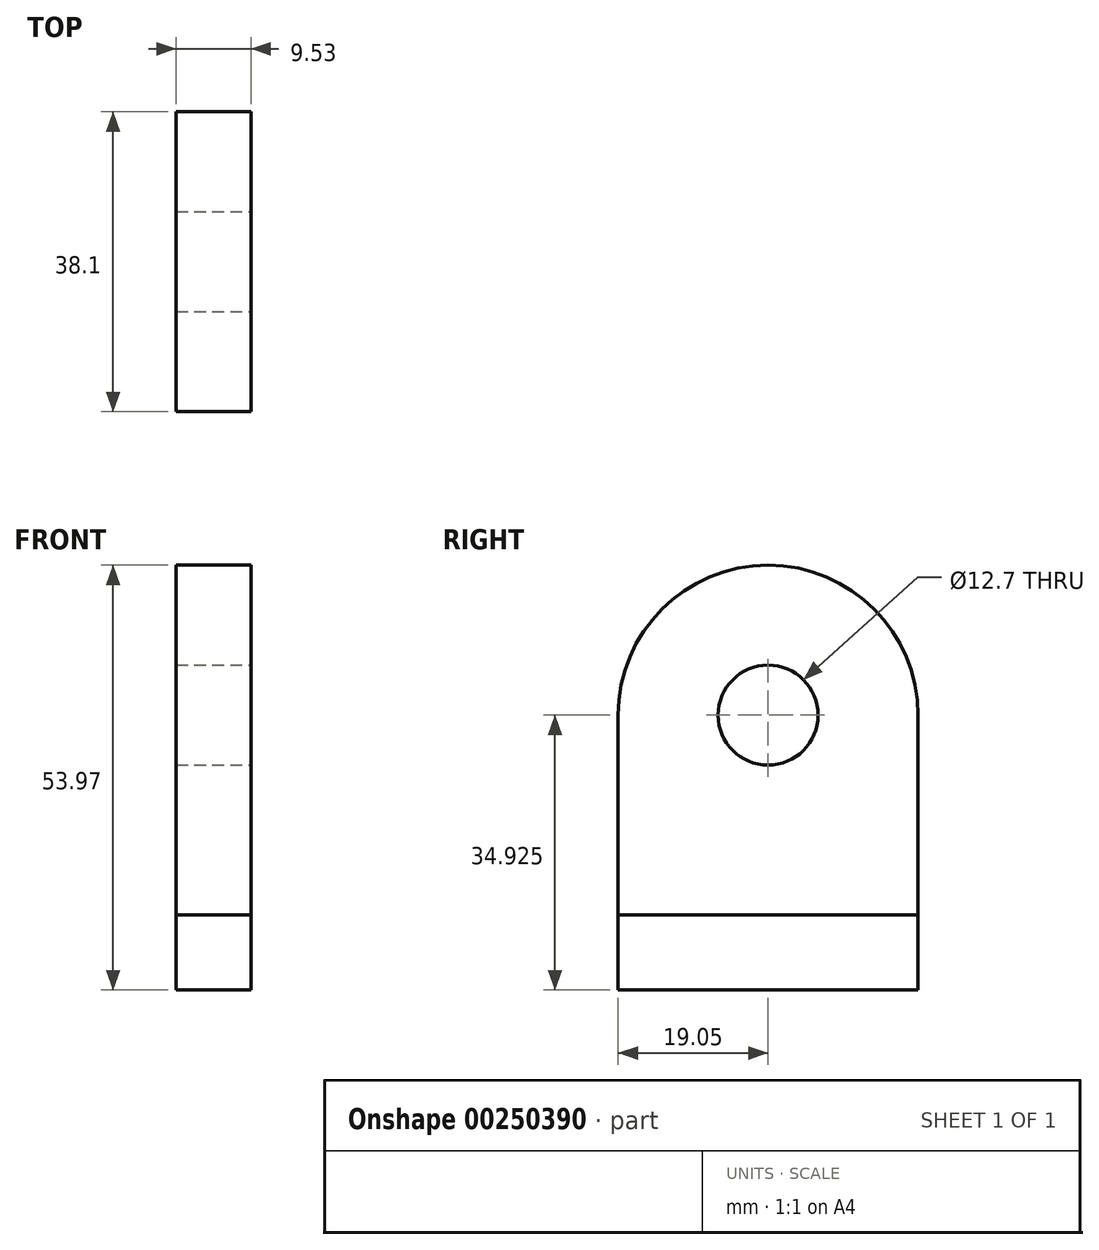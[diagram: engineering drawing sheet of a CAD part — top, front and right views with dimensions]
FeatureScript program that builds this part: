
annotation { "Feature Type Name" : "Feature", "Feature Type Description" : "" }
export const myFeature = defineFeature(function(context is Context, id is Id, definition is map)
    precondition{}
    {
        {
            var Q0;
            Q0=qCreatedBy(makeId("Top.planeOp"),FACE);
            var sketch = newSketch(context, id + "F0", { "sketchPlane" : qUnion([Q0])});
            skLineSegment(sketch, "E0", {"start": v(-57.12, 19.6) * mm, "end": v(3.2, 19.6) * mm});
            skLineSegment(sketch, "E1", {"start": v(3.2, -18.5) * mm, "end": v(-57.12, -18.5) * mm});
            skLineSegment(sketch, "E2", {"start": v(-57.12, 19.6) * mm, "end": v(-31.72, 19.6) * mm});
            skLineSegment(sketch, "E3", {"start": v(-31.72, 19.6) * mm, "end": v(-31.72, -18.5) * mm});
            skLineSegment(sketch, "E4", {"start": v(-31.72, -18.5) * mm, "end": v(-22.2, -18.5) * mm});
            skLineSegment(sketch, "E5", {"start": v(-22.2, -18.5) * mm, "end": v(-22.2, 19.6) * mm});
            skLineSegment(sketch, "E6", {"start": v(-22.2, 19.6) * mm, "end": v(-31.72, 19.6) * mm});
            skPoint(sketch, "E7.endSnap0", {"position": v(-76.17, 0.54) * mm});
            skArc(sketch, "E8", {"start": v(-57.12, 19.6) * mm, "mid": v(-70.59, 14.01) * mm, "end": v(-76.17, 0.54) * mm});
            skArc(sketch, "E9", {"start": v(-76.17, 0.54) * mm, "mid": v(-70.59, -12.93) * mm, "end": v(-57.12, -18.5) * mm});
            skArc(sketch, "E10", {"start": v(22.26, 0.54) * mm, "mid": v(16.68, 14.01) * mm, "end": v(3.2, 19.6) * mm});
            skArc(sketch, "E11", {"start": v(3.2, -18.5) * mm, "mid": v(16.68, -12.93) * mm, "end": v(22.26, 0.54) * mm});
            skPoint(sketch, "E12.orphan", {"position": v(-76.17, 19.6) * mm});
            skPoint(sketch, "E13.orphan", {"position": v(-76.17, -18.5) * mm});
            skPoint(sketch, "E14.orphan", {"position": v(22.26, -18.5) * mm});
            skPoint(sketch, "E15.orphan", {"position": v(22.26, 19.6) * mm});
            skSolve(sketch);
        }
        {
            var Q0;
            Q0=makeQuery(id+"F0.imprint","IMPRINT",FACE,{"disambiguationData":[TD([[makeQuery(id+"F0.imprint","IMPRINT",EDGE,{"derivedFrom":sQuery(id+"F0.wireOp",EDGE,"E0")}),-1.0]])]});
            var Q1;
            Q1=makeQuery(id+"F0.imprint","IMPRINT",FACE,{"disambiguationData":[TD([[makeQuery(id+"F0.imprint","IMPRINT",EDGE,{"derivedFrom":sQuery(id+"F0.wireOp",EDGE,"E2")}),-1.0]])]});
            extrude(context, id + "F1", {"entities" : qUnion([Q0, Q1]), "depth" : 9.52 * mm});
        }
        {
            var Q0;
            Q0=makeQuery(id+"F0.imprint","IMPRINT",FACE,{"disambiguationData":[TD([[makeQuery(id+"F0.imprint","IMPRINT",EDGE,{"derivedFrom":sQuery(id+"F0.wireOp",EDGE,"E3")}),1.0]])]});
            extrude(context, id + "F2", {"entities" : qUnion([Q0]), "depth" : 53.97 * mm});
        }
        {
            var Q0;
            Q0=makeQuery(id+"F2.opExtrude","SWEPT_FACE",FACE,{"disambiguationData":[OSD([sQuery(id+"F0.wireOp",EDGE,"E5")])]});
            var sketch = newSketch(context, id + "F3", { "sketchPlane" : qUnion([Q0])});
            skArc(sketch, "E16", {"start": v(19.6, 34.92) * mm, "mid": v(14.01, 48.4) * mm, "end": v(0.54, 53.98) * mm});
            skArc(sketch, "E17", {"start": v(0.54, 53.98) * mm, "mid": v(-12.93, 48.4) * mm, "end": v(-18.5, 34.92) * mm});
            skPoint(sketch, "E18.end.orphan", {"position": v(0.54, 34.92) * mm});
            skSolve(sketch);
        }
        {
            var Q0;
            {var subQ0=sQuery(id+"F3.wireOp",EDGE,"E17");Q0=makeQuery(id+"F3.imprint","IMPRINT",FACE,{"disambiguationData":[TD([[makeQuery(id+"F3.imprint","IMPRINT",EDGE,{"derivedFrom":subQ0}),-1.0]])]});}
            var Q1;
            {var subQ0=sQuery(id+"F3.wireOp",EDGE,"E16");Q1=makeQuery(id+"F3.imprint","IMPRINT",FACE,{"disambiguationData":[TD([[makeQuery(id+"F3.imprint","IMPRINT",EDGE,{"derivedFrom":subQ0}),-1.0]])]});}
            extrude(context, id + "F4", {"entities" : qUnion([Q0, Q1]), "operationType" : NewBodyOperationType.REMOVE, "oppositeDirection" : true, "depth" : 25.4 * mm});
        }
        {
            var Q0;
            Q0=sQuery(id+"F0.wireOp",VERTEX,"E8.center");
            var Q1;
            Q1=makeQuery(id+"F1.opExtrude","SWEPT_BODY",BODY,{"disambiguationData":[OSD([sQuery(id+"F0.wireOp",EDGE,"E1"),sQuery(id+"F0.wireOp",EDGE,"E2"),sQuery(id+"F0.wireOp",EDGE,"E3"),sQuery(id+"F0.wireOp",EDGE,"E8"),sQuery(id+"F0.wireOp",EDGE,"E9")])]});
            hole(context, id + "F5", {"style" : HoleStyle.SIMPLE, "endStyle" : HoleEndStyle.THROUGH, "oppositeDirection" : true, "holeDiameter" : 12.7 * mm, "tappedDepth" : 12.7 * mm, "tapClearance" : 3, "locations" : qUnion([Q0]), "scope" : qUnion([Q1])});
        }
        {
            var Q0;
            Q0=sQuery(id+"F0.wireOp",VERTEX,"E10.center");
            var Q1;
            Q1=makeQuery(id+"F1.opExtrude","SWEPT_BODY",BODY,{"disambiguationData":[OSD([sQuery(id+"F0.wireOp",EDGE,"E0"),sQuery(id+"F0.wireOp",EDGE,"E1"),sQuery(id+"F0.wireOp",EDGE,"E5"),sQuery(id+"F0.wireOp",EDGE,"E10"),sQuery(id+"F0.wireOp",EDGE,"E11")])]});
            hole(context, id + "F6", {"style" : HoleStyle.SIMPLE, "endStyle" : HoleEndStyle.THROUGH, "oppositeDirection" : true, "holeDiameter" : 12.7 * mm, "tappedDepth" : 12.7 * mm, "tapClearance" : 3, "locations" : qUnion([Q0]), "scope" : qUnion([Q1])});
        }
        {
            var Q0;
            Q0=makeQuery(id+"F2.opExtrude","SWEPT_FACE",FACE,{"disambiguationData":[OSD([sQuery(id+"F0.wireOp",EDGE,"E5")])]});
            var sketch = newSketch(context, id + "F7", { "sketchPlane" : qUnion([Q0])});
            skLineSegment(sketch, "E19", {"start": v(0.54, 53.98) * mm, "end": v(0.54, 34.93) * mm});
            skSolve(sketch);
        }
        {
            var Q0;
            Q0=sQuery(id+"F7.wireOp",VERTEX,"E19.end");
            var Q1;
            Q1=makeQuery(id+"F2.opExtrude","SWEPT_BODY",BODY,{"disambiguationData":[OSD([sQuery(id+"F0.wireOp",EDGE,"E3"),sQuery(id+"F0.wireOp",EDGE,"E4"),sQuery(id+"F0.wireOp",EDGE,"E5"),sQuery(id+"F0.wireOp",EDGE,"E6")])]});
            hole(context, id + "F8", {"style" : HoleStyle.SIMPLE, "endStyle" : HoleEndStyle.THROUGH, "holeDiameter" : 12.7 * mm, "tappedDepth" : 12.7 * mm, "tapClearance" : 3, "locations" : qUnion([Q0]), "scope" : qUnion([Q1])});
        }
    });
